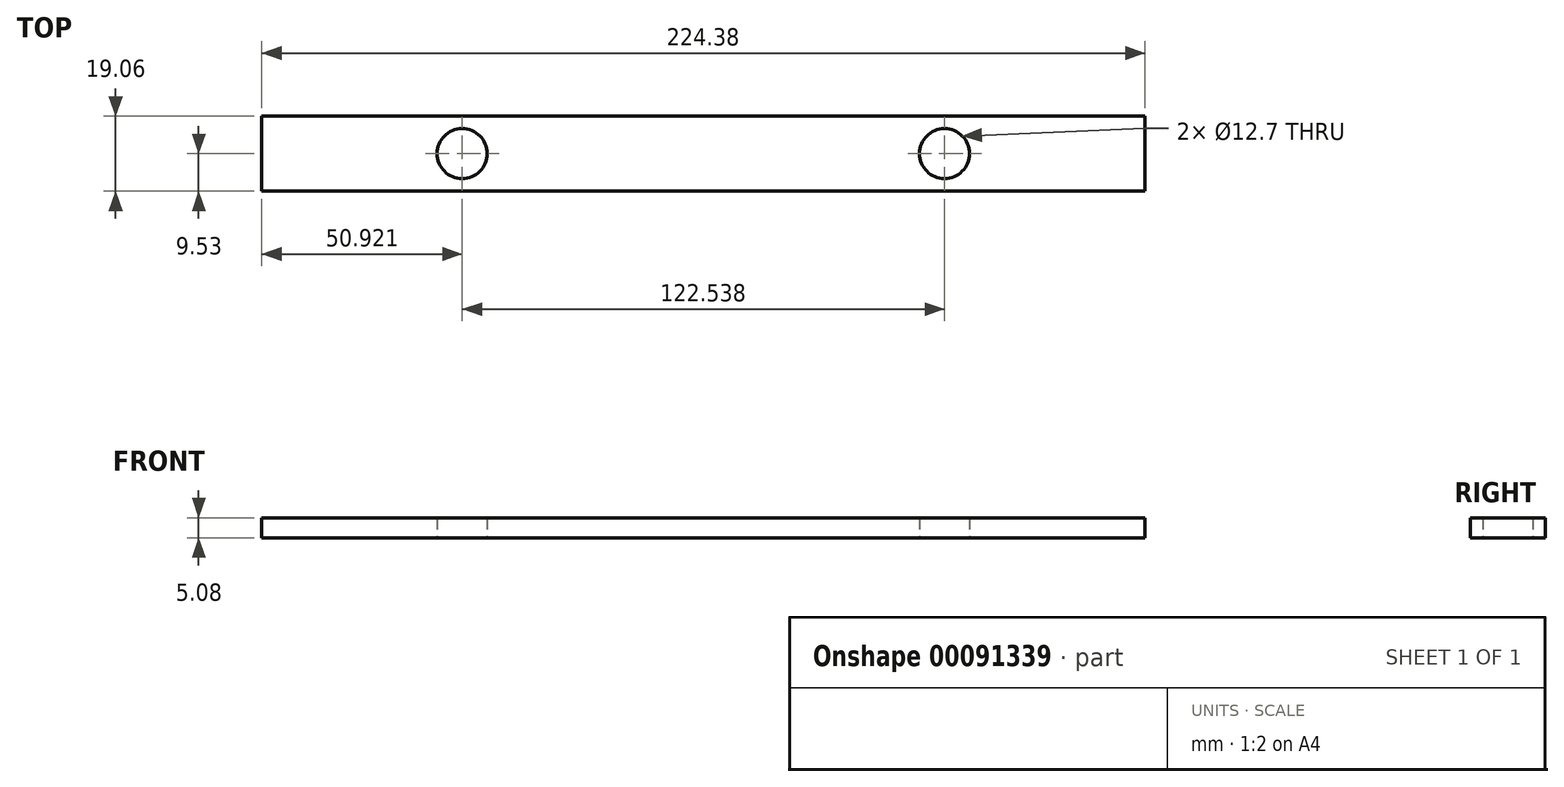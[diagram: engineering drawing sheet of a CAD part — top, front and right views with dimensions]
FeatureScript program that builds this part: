
annotation { "Feature Type Name" : "Feature", "Feature Type Description" : "" }
export const myFeature = defineFeature(function(context is Context, id is Id, definition is map)
    precondition{}
    {
        {
            var Q0;
            Q0=qCreatedBy(makeId("Top.planeOp"),FACE);
            var sketch = newSketch(context, id + "F0", { "sketchPlane" : qUnion([Q0])});
            skLineSegment(sketch, "E0.bottom", {"start": v(-61.27, 9.52) * mm, "end": v(61.27, 9.52) * mm});
            skLineSegment(sketch, "E0.top", {"start": v(-61.27, -9.52) * mm, "end": v(61.27, -9.52) * mm});
            skPoint(sketch, "E0.middle", {"position": v(0, 0) * mm});
            skCircle(sketch, "E1", {"center": v(-61.27, 0) * mm, "radius": 6.35 * mm});
            skCircle(sketch, "E2", {"center": v(61.27, 0) * mm, "radius": 6.35 * mm});
            skLineSegment(sketch, "E3.bottom", {"start": v(-112.19, 9.52) * mm, "end": v(-61.27, 9.52) * mm});
            skLineSegment(sketch, "E3.top", {"start": v(-112.19, -9.52) * mm, "end": v(-61.27, -9.52) * mm});
            skLineSegment(sketch, "E3.left", {"start": v(-112.19, 9.52) * mm, "end": v(-112.19, -9.52) * mm});
            skLineSegment(sketch, "E3.right", {"start": v(112.19, 9.52) * mm, "end": v(112.19, -9.52) * mm});
            skLineSegment(sketch, "E4.trimOffspring", {"start": v(61.27, 9.52) * mm, "end": v(112.19, 9.52) * mm});
            skLineSegment(sketch, "E5.trimOffspring", {"start": v(61.27, -9.52) * mm, "end": v(112.19, -9.52) * mm});
            skSolve(sketch);
        }
        {
            var Q0;
            Q0=makeQuery(id+"F0.imprint","IMPRINT",FACE,{"disambiguationData":[TD([[makeQuery(id+"F0.imprint","IMPRINT",EDGE,{"derivedFrom":sQuery(id+"F0.wireOp",EDGE,"E0.bottom")}),-1.0]])]});
            extrude(context, id + "F1", {"entities" : qUnion([Q0]), "depth" : 5.08 * mm});
        }
    });
